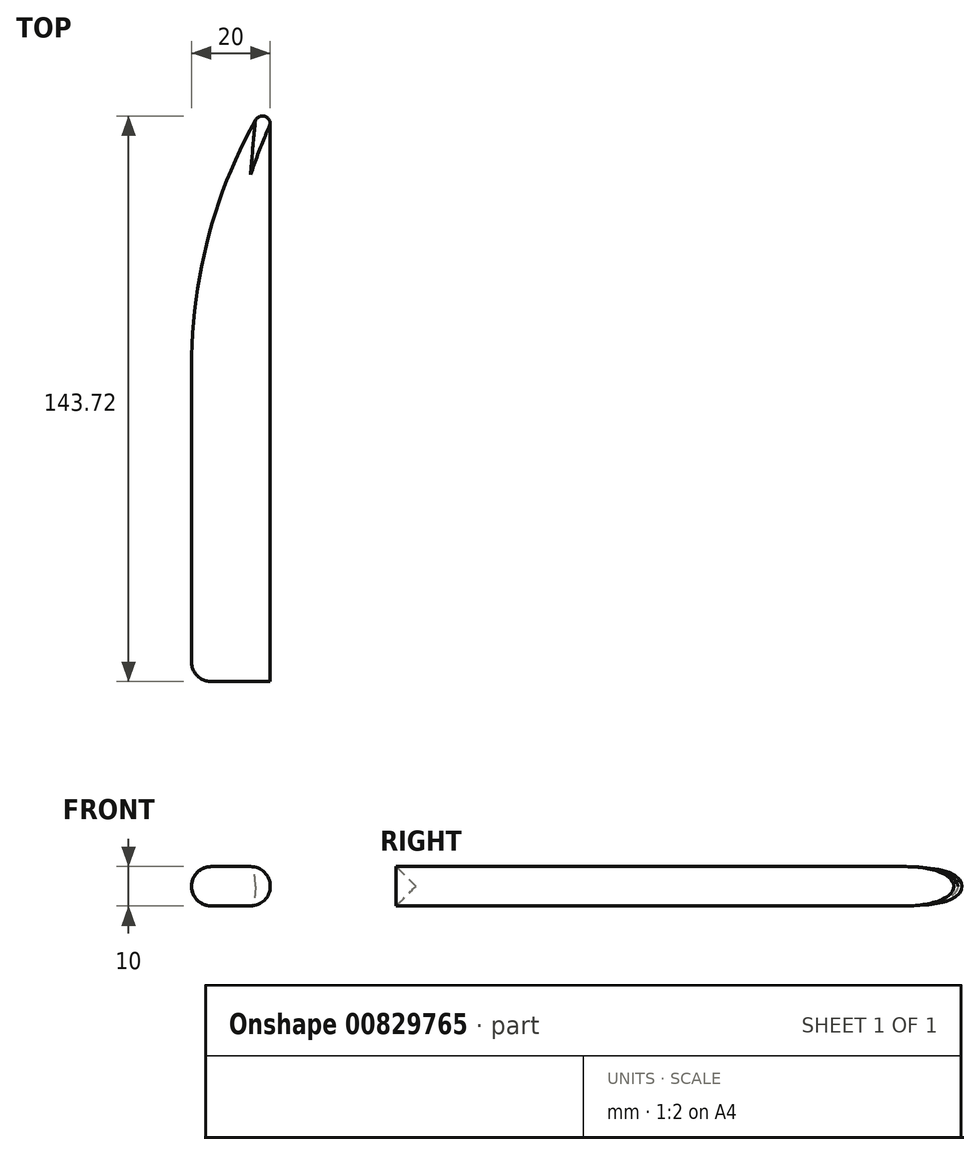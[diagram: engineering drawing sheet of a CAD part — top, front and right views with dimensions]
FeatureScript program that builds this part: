
annotation { "Feature Type Name" : "Feature", "Feature Type Description" : "" }
export const myFeature = defineFeature(function(context is Context, id is Id, definition is map)
    precondition{}
    {
        {
            var Q0;
            Q0=qCreatedBy(makeId("Top.planeOp"),FACE);
            var sketch = newSketch(context, id + "F0", { "sketchPlane" : qUnion([Q0])});
            skLineSegment(sketch, "E0.bottom", {"start": v(-10, 0) * mm, "end": v(10, 0) * mm});
            skLineSegment(sketch, "E0.top", {"start": v(-10, -80) * mm, "end": v(10, -80) * mm});
            skLineSegment(sketch, "E0.left", {"start": v(-10, 0) * mm, "end": v(-10, -80) * mm});
            skLineSegment(sketch, "E0.right", {"start": v(10, 0) * mm, "end": v(10, -80) * mm});
            skPoint(sketch, "E0.middle", {"position": v(0, -40) * mm});
            skLineSegment(sketch, "E1", {"start": v(10, 0) * mm, "end": v(10, 69) * mm});
            skArc(sketch, "E2", {"start": v(10, 69) * mm, "mid": v(-4.9, 35.92) * mm, "end": v(-10, 0) * mm});
            skSolve(sketch);
        }
        {
            var Q0;
            Q0 = qSketchRegion(id + "F0", true);
            extrude(context, id + "F1", {"entities" : qUnion([Q0]), "depth" : 10 * mm, "offsetDistance" : 25 * mm});
        }
        {
            var Q0;
            Q0=makeQuery(id+"F1.opExtrude","SWEPT_EDGE",EDGE,{"disambiguationData":[OSD([sQuery(id+"F0.wireOp",EDGE,"E1"),sQuery(id+"F0.wireOp",EDGE,"bmzHxQOi-kstd-LTul-vWBq-SWINP06bZMRP")])]});
            fillet(context, id + "F2", {"entities" : qUnion([Q0]), "radius" : 2 * mm, "tangentPropagation" : true, "allowEdgeOverflow" : false});
        }
        {
            var Q0;
            Q0=makeQuery(id+"F1.opExtrude","SWEPT_FACE",FACE,{"disambiguationData":[OSD([sQuery(id+"F0.wireOp",EDGE,"E0.left")])]});
            fillet(context, id + "F3", {"entities" : qUnion([Q0]), "radius" : 5 * mm, "tangentPropagation" : true, "allowEdgeOverflow" : false});
        }
    });
